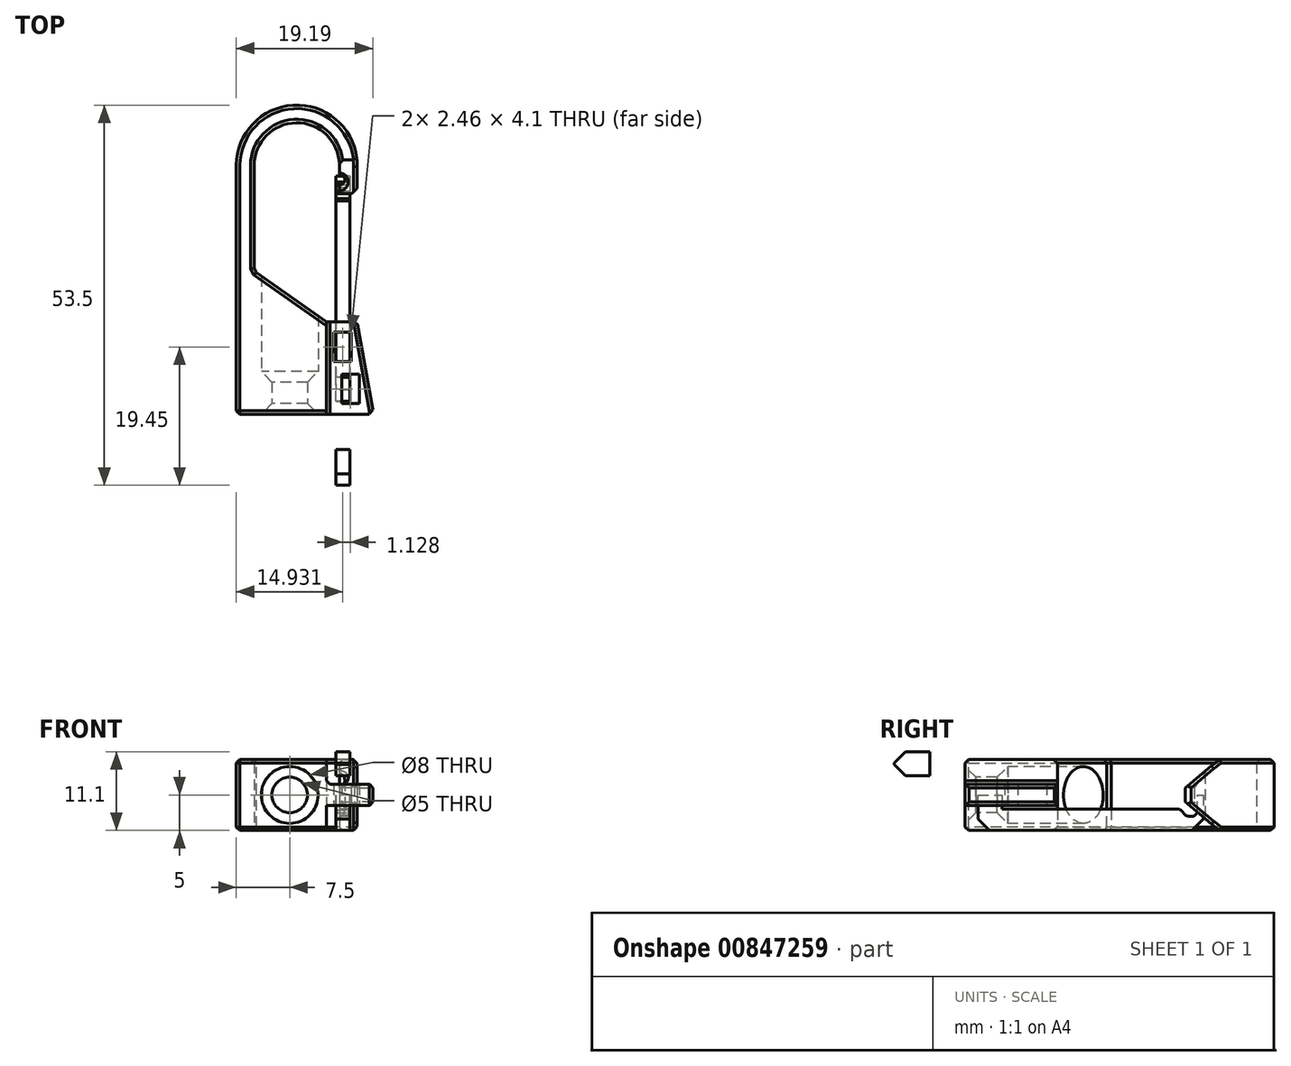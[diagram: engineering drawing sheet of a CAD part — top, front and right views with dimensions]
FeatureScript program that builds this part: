
annotation { "Feature Type Name" : "Feature", "Feature Type Description" : "" }
export const myFeature = defineFeature(function(context is Context, id is Id, definition is map)
    precondition{}
    {
        {
            var Q0;
            Q0=qCreatedBy(makeId("Top.planeOp"),FACE);
            var sketch = newSketch(context, id + "F0", { "sketchPlane" : qUnion([Q0])});
            skCircle(sketch, "E0", {"center": v(-1, -1.5) * mm, "radius": 4 * mm});
            skLineSegment(sketch, "E1.bottom", {"start": v(-8.5, 3.5) * mm, "end": v(8.5, 3.5) * mm});
            skLineSegment(sketch, "E1.top", {"start": v(-8.5, -6.5) * mm, "end": v(8.5, -6.5) * mm});
            skLineSegment(sketch, "E1.left", {"start": v(-8.5, 3.5) * mm, "end": v(-8.5, -6.5) * mm});
            skLineSegment(sketch, "E1.right", {"start": v(8.5, 3.5) * mm, "end": v(8.5, -6.5) * mm});
            skPoint(sketch, "E1.middle", {"position": v(0, -1.5) * mm});
            skCircle(sketch, "E2", {"center": v(-1, -1.5) * mm, "radius": 2.5 * mm});
            skSolve(sketch);
        }
        {
            var Q0;
            Q0=qCreatedBy(makeId("Front.planeOp"),FACE);
            cPlane(context, id + "F1", {"entities" : qUnion([Q0]), "cplaneType" : CPlaneType.OFFSET, "offset" : 3.5 * mm, "oppositeDirection" : true, "width" : 150 * mm, "height" : 150 * mm});
        }
        {
            var Q0;
            Q0=qCreatedBy(id+"F1.planeOp",FACE);
            var sketch = newSketch(context, id + "F2", { "sketchPlane" : qUnion([Q0])});
            skLineSegment(sketch, "E3", {"start": v(0, 0) * mm, "end": v(8.5, 0) * mm});
            skLineSegment(sketch, "E4.MirrorCS", {"start": v(0, 0) * mm, "end": v(-8.5, 0) * mm});
            skLineSegment(sketch, "E5", {"start": v(8.5, 0) * mm, "end": v(8.5, 13) * mm});
            skLineSegment(sketch, "E6", {"start": v(8.5, 13) * mm, "end": v(4.2, 13) * mm});
            skLineSegment(sketch, "E7", {"start": v(4.2, 13) * mm, "end": v(-6, 20.14) * mm});
            skLineSegment(sketch, "E8", {"start": v(-8.5, 0) * mm, "end": v(-8.5, 35) * mm});
            skLineSegment(sketch, "E9", {"start": v(-6, 20.14) * mm, "end": v(-6, 35) * mm});
            skLineSegment(sketch, "E10", {"start": v(-6, 35) * mm, "end": v(0, 35) * mm});
            skArc(sketch, "E11", {"start": v(8.5, 35) * mm, "mid": v(0, 43.5) * mm, "end": v(-8.5, 35) * mm});
            skArc(sketch, "E12", {"start": v(6, 35) * mm, "mid": v(0, 41) * mm, "end": v(-6, 35) * mm});
            skLineSegment(sketch, "E13", {"start": v(0, 35) * mm, "end": v(8.5, 35) * mm});
            skLineSegment(sketch, "E14", {"start": v(6, 35) * mm, "end": v(6, 31) * mm});
            skLineSegment(sketch, "E15.bottom", {"start": v(6, 31) * mm, "end": v(8.5, 31) * mm});
            skLineSegment(sketch, "E15.top", {"start": v(6, 35) * mm, "end": v(8.5, 35) * mm});
            skLineSegment(sketch, "E15.left", {"start": v(6, 31) * mm, "end": v(6, 35) * mm});
            skLineSegment(sketch, "E15.right", {"start": v(8.5, 31) * mm, "end": v(8.5, 35) * mm});
            skCircle(sketch, "E16", {"center": v(8.5, 33) * mm, "radius": 0.75 * mm});
            skLineSegment(sketch, "E17", {"start": v(8.5, 13) * mm, "end": v(10.8, 0) * mm});
            skLineSegment(sketch, "E18", {"start": v(10.8, 0) * mm, "end": v(8.5, 0) * mm});
            skLineSegment(sketch, "E19", {"start": v(4.2, 13) * mm, "end": v(4.2, 0) * mm});
            skLineSegment(sketch, "E20.0", {"start": v(5.2, 12) * mm, "end": v(5.2, 0) * mm});
            skLineSegment(sketch, "E20.1", {"start": v(7.66, 12) * mm, "end": v(5.2, 12) * mm});
            skLineSegment(sketch, "E20.2", {"start": v(7.66, 12) * mm, "end": v(9.6, 1) * mm});
            skLineSegment(sketch, "E20.3", {"start": v(9.6, 1) * mm, "end": v(8.5, 1) * mm});
            skLineSegment(sketch, "E21", {"start": v(8.5, 1) * mm, "end": v(5.2, 1) * mm});
            skLineSegment(sketch, "E22", {"start": v(5.2, 12) * mm, "end": v(7.14, 1) * mm});
            skCircle(sketch, "E23", {"center": v(6, 33) * mm, "radius": 0.75 * mm});
            skLineSegment(sketch, "E24.0", {"start": v(8.5, 11.5) * mm, "end": v(4.2, 11.5) * mm});
            skLineSegment(sketch, "E25.0", {"start": v(0, 1.5) * mm, "end": v(8.5, 1.5) * mm});
            skLineSegment(sketch, "E25.1", {"start": v(10.8, 1.5) * mm, "end": v(8.5, 1.5) * mm});
            skLineSegment(sketch, "E26", {"start": v(8.79, 5.6) * mm, "end": v(8.79, 1) * mm});
            skLineSegment(sketch, "E27", {"start": v(8.79, 5.6) * mm, "end": v(6.33, 5.6) * mm});
            skLineSegment(sketch, "E28", {"start": v(7.66, 12) * mm, "end": v(7.66, 7.4) * mm});
            skLineSegment(sketch, "E29", {"start": v(7.66, 7.4) * mm, "end": v(5.2, 7.4) * mm});
            skLineSegment(sketch, "E30", {"start": v(6.33, 5.6) * mm, "end": v(6.33, 1) * mm});
            skSolve(sketch);
        }
        {
            var Q0;
            {var subQ1=sQuery(id+"F2.wireOp",EDGE,"E6");Q0=makeQuery(id+"F2.imprint","IMPRINT",FACE,{"disambiguationData":[TD([[makeQuery(id+"F2.imprint","IMPRINT",EDGE,{"derivedFrom":subQ1}),1.0]])]});}
            var Q1;
            {var subQ0=sQuery(id+"F2.wireOp",EDGE,"E24.0");var subQ1=sQuery(id+"F2.wireOp",EDGE,"E19");var subQ2=makeQuery(id+"F2.imprint","INTERSECT",VERTEX,{"derivedFrom":[subQ1,subQ0]});Q1=makeQuery(id+"F2.imprint","IMPRINT",FACE,{"disambiguationData":[TD([[makeQuery(id+"F2.imprint","IMPRINT",EDGE,{"disambiguationData":[TD([[subQ2,-1.0]])],"derivedFrom":subQ1}),1.0]])]});}
            var Q2;
            {var subQ4=sQuery(id+"F2.wireOp",EDGE,"E3");var subQ6=sQuery(id+"F2.wireOp",EDGE,"E19");var subQ7=makeQuery(id+"F2.imprint","INTERSECT",VERTEX,{"derivedFrom":[subQ4,subQ6]});Q2=makeQuery(id+"F2.imprint","IMPRINT",FACE,{"disambiguationData":[TD([[makeQuery(id+"F2.imprint","IMPRINT",EDGE,{"disambiguationData":[TD([[subQ7,-1.0]])],"derivedFrom":subQ4}),1.0]])]});}
            var Q3;
            {var subQ0=sQuery(id+"F2.wireOp",EDGE,"E20.0");var subQ1=sQuery(id+"F2.wireOp",EDGE,"E3");var subQ2=makeQuery(id+"F2.imprint","INTERSECT",VERTEX,{"derivedFrom":[subQ1,subQ0]});Q3=makeQuery(id+"F2.imprint","IMPRINT",FACE,{"disambiguationData":[TD([[makeQuery(id+"F2.imprint","IMPRINT",EDGE,{"disambiguationData":[TD([[subQ2,1.0]])],"derivedFrom":subQ0}),1.0]])]});}
            var Q4;
            {var subQ0=sQuery(id+"F2.wireOp",EDGE,"E18");Q4=makeQuery(id+"F2.imprint","IMPRINT",FACE,{"disambiguationData":[TD([[makeQuery(id+"F2.imprint","IMPRINT",EDGE,{"derivedFrom":subQ0}),-1.0]])]});}
            var Q5;
            {var subQ2=sQuery(id+"F2.wireOp",EDGE,"E5");var subQ6=makeQuery(id+"F2.imprint","INTERSECT",VERTEX,{"derivedFrom":[subQ2,sQuery(id+"F2.wireOp",EDGE,"E24.0")]});Q5=makeQuery(id+"F2.imprint","IMPRINT",FACE,{"disambiguationData":[TD([[makeQuery(id+"F2.imprint","IMPRINT",EDGE,{"disambiguationData":[TD([[subQ6,1.0]])],"derivedFrom":subQ2}),-1.0]])]});}
            var Q6;
            {var subQ4=sQuery(id+"F2.wireOp",EDGE,"E4.MirrorCS");Q6=makeQuery(id+"F2.imprint","IMPRINT",FACE,{"disambiguationData":[TD([[makeQuery(id+"F2.imprint","IMPRINT",EDGE,{"derivedFrom":subQ4}),-1.0]])]});}
            var Q7;
            {var subQ5=sQuery(id+"F2.wireOp",EDGE,"E5");var subQ7=sQuery(id+"F2.wireOp",EDGE,"E27");var subQ13=makeQuery(id+"F2.imprint","INTERSECT",VERTEX,{"derivedFrom":[subQ5,subQ7]});Q7=makeQuery(id+"F2.imprint","IMPRINT",FACE,{"disambiguationData":[TD([[makeQuery(id+"F2.imprint","IMPRINT",EDGE,{"disambiguationData":[TD([[subQ13,-1.0]])],"derivedFrom":subQ5}),1.0]])]});}
            var Q8;
            {var subQ1=sQuery(id+"F2.wireOp",EDGE,"E20.0");var subQ7=sQuery(id+"F2.wireOp",EDGE,"E29");var subQ9=makeQuery(id+"F2.imprint","INTERSECT",VERTEX,{"derivedFrom":[subQ1,subQ7]});Q8=makeQuery(id+"F2.imprint","IMPRINT",FACE,{"disambiguationData":[TD([[makeQuery(id+"F2.imprint","IMPRINT",EDGE,{"disambiguationData":[TD([[subQ9,-1.0]])],"derivedFrom":subQ1}),1.0]])]});}
            var Q9;
            {var subQ1=sQuery(id+"F2.wireOp",EDGE,"E20.2");var subQ3=sQuery(id+"F2.wireOp",EDGE,"E24.0");var subQ4=makeQuery(id+"F2.imprint","INTERSECT",VERTEX,{"derivedFrom":[subQ1,subQ3]});Q9=makeQuery(id+"F2.imprint","IMPRINT",FACE,{"disambiguationData":[TD([[makeQuery(id+"F2.imprint","IMPRINT",EDGE,{"disambiguationData":[TD([[subQ4,-1.0]])],"derivedFrom":subQ3}),-1.0]])]});}
            var Q10;
            {var subQ0=sQuery(id+"F2.wireOp",EDGE,"E24.0");var subQ1=sQuery(id+"F2.wireOp",EDGE,"E5");var subQ2=makeQuery(id+"F2.imprint","INTERSECT",VERTEX,{"derivedFrom":[subQ1,subQ0]});Q10=makeQuery(id+"F2.imprint","IMPRINT",FACE,{"disambiguationData":[TD([[makeQuery(id+"F2.imprint","IMPRINT",EDGE,{"disambiguationData":[TD([[subQ2,1.0]])],"derivedFrom":subQ1}),1.0]])]});}
            var Q11;
            {var subQ0=sQuery(id+"F2.wireOp",EDGE,"E21");var subQ1=sQuery(id+"F2.wireOp",EDGE,"E20.0");var subQ2=makeQuery(id+"F2.imprint","INTERSECT",VERTEX,{"derivedFrom":[subQ1,subQ0]});Q11=makeQuery(id+"F2.imprint","IMPRINT",FACE,{"disambiguationData":[TD([[makeQuery(id+"F2.imprint","IMPRINT",EDGE,{"disambiguationData":[TD([[subQ2,1.0]])],"derivedFrom":subQ1}),1.0]])]});}
            var Q12;
            {var subQ4=sQuery(id+"F2.wireOp",EDGE,"E15.bottom");Q12=makeQuery(id+"F2.imprint","IMPRINT",FACE,{"disambiguationData":[TD([[makeQuery(id+"F2.imprint","IMPRINT",EDGE,{"derivedFrom":subQ4}),1.0]])]});}
            var Q13;
            {var subQ0=sQuery(id+"F2.wireOp",EDGE,"E16");var subQ1=sQuery(id+"F2.wireOp",EDGE,"E15.right");var subQ2=makeQuery(id+"F2.imprint","INTERSECT",VERTEX,{"disambiguationData":[OD(0.0)],"derivedFrom":[subQ1,subQ0]});Q13=makeQuery(id+"F2.imprint","IMPRINT",FACE,{"disambiguationData":[TD([[makeQuery(id+"F2.imprint","IMPRINT",EDGE,{"disambiguationData":[TD([[subQ2,-1.0]])],"derivedFrom":subQ1}),1.0]])]});}
            var Q14;
            {var subQ1=sQuery(id+"F2.wireOp",EDGE,"E20.2");var subQ3=sQuery(id+"F2.wireOp",EDGE,"E25.1");var subQ4=makeQuery(id+"F2.imprint","INTERSECT",VERTEX,{"derivedFrom":[subQ1,subQ3]});Q14=makeQuery(id+"F2.imprint","IMPRINT",FACE,{"disambiguationData":[TD([[makeQuery(id+"F2.imprint","IMPRINT",EDGE,{"disambiguationData":[TD([[subQ4,-1.0]])],"derivedFrom":subQ3}),-1.0]])]});}
            var Q15;
            {var subQ0=sQuery(id+"F2.wireOp",EDGE,"E20.3");var subQ1=sQuery(id+"F2.wireOp",EDGE,"E20.2");var subQ2=makeQuery(id+"F2.imprint","INTERSECT",VERTEX,{"derivedFrom":[subQ1,subQ0]});Q15=makeQuery(id+"F2.imprint","IMPRINT",FACE,{"disambiguationData":[TD([[makeQuery(id+"F2.imprint","IMPRINT",EDGE,{"disambiguationData":[TD([[subQ2,1.0]])],"derivedFrom":subQ1}),-1.0]])]});}
            var Q16;
            {var subQ0=sQuery(id+"F2.wireOp",EDGE,"E27");var subQ1=sQuery(id+"F2.wireOp",EDGE,"E5");var subQ2=makeQuery(id+"F2.imprint","INTERSECT",VERTEX,{"derivedFrom":[subQ1,subQ0]});Q16=makeQuery(id+"F2.imprint","IMPRINT",FACE,{"disambiguationData":[TD([[makeQuery(id+"F2.imprint","IMPRINT",EDGE,{"disambiguationData":[TD([[subQ2,-1.0]])],"derivedFrom":subQ1}),-1.0]])]});}
            var Q17;
            {var subQ0=sQuery(id+"F2.wireOp",EDGE,"E22");var subQ1=sQuery(id+"F2.wireOp",EDGE,"E21");var subQ2=makeQuery(id+"F2.imprint","INTERSECT",VERTEX,{"derivedFrom":[subQ1,subQ0]});Q17=makeQuery(id+"F2.imprint","IMPRINT",FACE,{"disambiguationData":[TD([[makeQuery(id+"F2.imprint","IMPRINT",EDGE,{"disambiguationData":[TD([[subQ2,-1.0]])],"derivedFrom":subQ1}),-1.0]])]});}
            var Q18;
            {var subQ0=sQuery(id+"F2.wireOp",EDGE,"E21");var subQ5=sQuery(id+"F2.wireOp",EDGE,"E22");var subQ7=makeQuery(id+"F2.imprint","INTERSECT",VERTEX,{"derivedFrom":[subQ0,subQ5]});Q18=makeQuery(id+"F2.imprint","IMPRINT",FACE,{"disambiguationData":[TD([[makeQuery(id+"F2.imprint","IMPRINT",EDGE,{"disambiguationData":[TD([[subQ7,1.0]])],"derivedFrom":subQ5}),1.0]])]});}
            var Q19;
            {var subQ0=sQuery(id+"F2.wireOp",EDGE,"E20.3");var subQ5=sQuery(id+"F2.wireOp",EDGE,"E26");var subQ6=makeQuery(id+"F2.imprint","INTERSECT",VERTEX,{"derivedFrom":[subQ0,subQ5]});Q19=makeQuery(id+"F2.imprint","IMPRINT",FACE,{"disambiguationData":[TD([[makeQuery(id+"F2.imprint","IMPRINT",EDGE,{"disambiguationData":[TD([[subQ6,1.0]])],"derivedFrom":subQ5}),-1.0]])]});}
            var Q20;
            {var subQ0=sQuery(id+"F2.wireOp",EDGE,"E20.1");Q20=makeQuery(id+"F2.imprint","IMPRINT",FACE,{"disambiguationData":[TD([[makeQuery(id+"F2.imprint","IMPRINT",EDGE,{"derivedFrom":subQ0}),1.0]])]});}
            var Q21;
            {var subQ1=sQuery(id+"F2.wireOp",EDGE,"E20.0");var subQ3=sQuery(id+"F2.wireOp",EDGE,"E24.0");var subQ4=makeQuery(id+"F2.imprint","INTERSECT",VERTEX,{"derivedFrom":[subQ1,subQ3]});Q21=makeQuery(id+"F2.imprint","IMPRINT",FACE,{"disambiguationData":[TD([[makeQuery(id+"F2.imprint","IMPRINT",EDGE,{"disambiguationData":[TD([[subQ4,1.0]])],"derivedFrom":subQ3}),-1.0]])]});}
            var Q22;
            {var subQ1=sQuery(id+"F2.wireOp",EDGE,"E20.2");var subQ3=sQuery(id+"F2.wireOp",EDGE,"E24.0");var subQ4=makeQuery(id+"F2.imprint","INTERSECT",VERTEX,{"derivedFrom":[subQ1,subQ3]});Q22=makeQuery(id+"F2.imprint","IMPRINT",FACE,{"disambiguationData":[TD([[makeQuery(id+"F2.imprint","IMPRINT",EDGE,{"disambiguationData":[TD([[subQ4,-1.0]])],"derivedFrom":subQ3}),-1.0]])]});}
            extrude(context, id + "F3", {"entities" : qUnion([Q0, Q1, Q2, Q3, Q4, Q5, Q6, Q7, Q8, Q9, Q10, Q11, Q12, Q13, Q14, Q15, Q16, Q17, Q18, Q19, Q20, Q21, Q22]), "depth" : 10 * mm, "offsetDistance" : 25 * mm});
        }
        {
            var Q0;
            Q0=makeQuery(id+"F0.imprint","IMPRINT",FACE,{"disambiguationData":[TD([[makeQuery(id+"F0.imprint","IMPRINT",EDGE,{"derivedFrom":sQuery(id+"F0.wireOp",EDGE,"E0")}),1.0]])]});
            var Q1;
            Q1=makeQuery(id+"F0.imprint","IMPRINT",FACE,{"disambiguationData":[TD([[makeQuery(id+"F0.imprint","IMPRINT",EDGE,{"derivedFrom":sQuery(id+"F0.wireOp",EDGE,"E2")}),1.0]])]});
            extrude(context, id + "F4", {"entities" : qUnion([Q0, Q1]), "operationType" : NewBodyOperationType.REMOVE, "depth" : 25 * mm, "offsetDistance" : 25 * mm});
        }
        {
            var Q0;
            Q0=makeQuery(id+"F0.imprint","IMPRINT",FACE,{"disambiguationData":[TD([[makeQuery(id+"F0.imprint","IMPRINT",EDGE,{"derivedFrom":sQuery(id+"F0.wireOp",EDGE,"E0")}),1.0]])]});
            extrude(context, id + "F5", {"entities" : qUnion([Q0]), "operationType" : NewBodyOperationType.ADD, "depth" : 6 * mm, "offsetDistance" : 25 * mm});
        }
        {
            var Q0;
            Q0=makeQuery(id+"F3.opExtrude","CAP_EDGE",EDGE,{"disambiguationData":[OSD([sQuery(id+"F2.wireOp",EDGE,"E15.bottom")])],"isStart":false});
            var Q1;
            Q1=makeQuery(id+"F3.opExtrude","CAP_EDGE",EDGE,{"disambiguationData":[OSD([sQuery(id+"F2.wireOp",EDGE,"E15.bottom")])],"isStart":true});
            chamfer(context, id + "F6", {"entities" : qUnion([Q0, Q1]), "chamferType" : ChamferType.OFFSET_ANGLE, "width" : 4 * mm, "oppositeDirection" : true, "angle" : 50 * degree, "tangentPropagation" : true});
        }
        {
            var Q0;
            Q0=makeQuery(id+"F5.opExtrude","CAP_EDGE",EDGE,{"disambiguationData":[OSD([sQuery(id+"F0.wireOp",EDGE,"E2")])],"isStart":true});
            var Q1;
            Q1=makeQuery(id+"F5.opExtrude","CAP_EDGE",EDGE,{"disambiguationData":[OSD([sQuery(id+"F0.wireOp",EDGE,"E2")])],"isStart":false});
            chamfer(context, id + "F7", {"entities" : qUnion([Q0, Q1]), "width" : 1.5 * mm, "tangentPropagation" : true});
        }
        {
            var Q0;
            Q0=makeQuery(id+"F3.opExtrude","SWEPT_EDGE",EDGE,{"disambiguationData":[OSD([sQuery(id+"F2.wireOp",EDGE,"E7"),sQuery(id+"F2.wireOp",EDGE,"E9")])]});
            var Q1;
            Q1=makeQuery(id+"F3.opExtrude","SWEPT_EDGE",EDGE,{"disambiguationData":[OSD([sQuery(id+"F2.wireOp",EDGE,"E15.bottom"),sQuery(id+"F2.wireOp",EDGE,"E15.right")])]});
            chamfer(context, id + "F8", {"entities" : qUnion([Q0, Q1]), "width" : .8 * mm, "tangentPropagation" : true});
        }
        {
            var Q0;
            Q0=qCreatedBy(id+"F1.planeOp",FACE);
            var sketch = newSketch(context, id + "F9", { "sketchPlane" : qUnion([Q0])});
            skLineSegment(sketch, "E31", {"start": v(0, 0) * mm, "end": v(4.2, 0) * mm});
            skLineSegment(sketch, "E32", {"start": v(4.2, 0) * mm, "end": v(11.2, 0) * mm});
            skLineSegment(sketch, "E33", {"start": v(4.2, 0) * mm, "end": v(4.2, 15.17) * mm});
            skLineSegment(sketch, "E34.bottom", {"start": v(4.2, 15.17) * mm, "end": v(11.2, 15.17) * mm});
            skLineSegment(sketch, "E34.left", {"start": v(4.2, 15.17) * mm, "end": v(4.2, 0) * mm});
            skLineSegment(sketch, "E34.right", {"start": v(11.2, 15.17) * mm, "end": v(11.2, 0) * mm});
            skSolve(sketch);
        }
        {
            var Q0;
            Q0=qSketchRegion(id+"F9",true);
            extrude(context, id + "F10", {"entities" : qUnion([Q0]), "operationType" : NewBodyOperationType.REMOVE, "depth" : 3.5 * mm, "offsetDistance" : 25 * mm});
        }
        {
            var Q0;
            Q0=qCreatedBy(id+"F1.planeOp",FACE);
            cPlane(context, id + "F11", {"entities" : qUnion([Q0]), "cplaneType" : CPlaneType.OFFSET, "offset" : 10 * mm, "width" : 150 * mm, "height" : 150 * mm});
        }
        {
            var Q0;
            Q0=qCreatedBy(id+"F11.planeOp",FACE);
            var sketch = newSketch(context, id + "F12", { "sketchPlane" : qUnion([Q0])});
            skLineSegment(sketch, "E35", {"start": v(0, 0) * mm, "end": v(4.2, 0) * mm});
            skLineSegment(sketch, "E36", {"start": v(4.2, 0) * mm, "end": v(11.2, 0) * mm});
            skLineSegment(sketch, "E37", {"start": v(11.2, 0) * mm, "end": v(11.2, 14.54) * mm});
            skLineSegment(sketch, "E38.bottom", {"start": v(11.2, 14.54) * mm, "end": v(4.2, 14.54) * mm});
            skLineSegment(sketch, "E38.top", {"start": v(11.2, 0) * mm, "end": v(4.2, 0) * mm});
            skLineSegment(sketch, "E38.left", {"start": v(11.2, 14.54) * mm, "end": v(11.2, 0) * mm});
            skLineSegment(sketch, "E38.right", {"start": v(4.2, 14.54) * mm, "end": v(4.2, 0) * mm});
            skSolve(sketch);
        }
        {
            var Q0;
            Q0=qSketchRegion(id+"F12",true);
            extrude(context, id + "F13", {"entities" : qUnion([Q0]), "operationType" : NewBodyOperationType.REMOVE, "oppositeDirection" : true, "depth" : 3.5 * mm, "offsetDistance" : 25 * mm});
        }
        {
            var Q0;
            Q0=makeQuery(id+"F13.boolean.opBoolean","INTERSECT",EDGE,{"derivedFrom":[makeQuery(id+"F3.opExtrude","SWEPT_FACE",FACE,{"disambiguationData":[OSD([sQuery(id+"F2.wireOp",EDGE,"E17")])]}),makeQuery(id+"F13.opExtrude","CAP_FACE",FACE,{"disambiguationData":[OSD([sQuery(id+"F12.wireOp",EDGE,"E38.bottom"),sQuery(id+"F12.wireOp",EDGE,"E38.top"),sQuery(id+"F12.wireOp",EDGE,"E38.left"),sQuery(id+"F12.wireOp",EDGE,"E38.right")])],"isStart":false})]});
            var Q1;
            Q1=makeQuery(id+"F10.boolean.opBoolean","INTERSECT",EDGE,{"derivedFrom":[makeQuery(id+"F3.opExtrude","SWEPT_FACE",FACE,{"disambiguationData":[OSD([sQuery(id+"F2.wireOp",EDGE,"E17")])]}),makeQuery(id+"F10.opExtrude","CAP_FACE",FACE,{"disambiguationData":[OSD([sQuery(id+"F9.wireOp",EDGE,"E34.bottom"),sQuery(id+"F9.wireOp",EDGE,"E32"),sQuery(id+"F9.wireOp",EDGE,"E34.left"),sQuery(id+"F9.wireOp",EDGE,"E34.right")])],"isStart":false})]});
            var Q2;
            Q2=makeQuery(id+"F3.opExtrude","CAP_EDGE",EDGE,{"disambiguationData":[OSD([sQuery(id+"F2.wireOp",EDGE,"E8")])],"isStart":false});
            var Q3;
            Q3=makeQuery(id+"F3.opExtrude","CAP_EDGE",EDGE,{"disambiguationData":[OSD([sQuery(id+"F2.wireOp",EDGE,"E8")])],"isStart":true});
            var Q4;
            Q4=makeQuery(id+"F3.opExtrude","CAP_EDGE",EDGE,{"disambiguationData":[OSD([sQuery(id+"F2.wireOp",EDGE,"E9")])],"isStart":true});
            var Q5;
            Q5=makeQuery(id+"F3.opExtrude","CAP_EDGE",EDGE,{"disambiguationData":[OSD([sQuery(id+"F2.wireOp",EDGE,"E9")])],"isStart":false});
            var Q6;
            Q6=makeQuery(id+"F3.opExtrude","CAP_EDGE",EDGE,{"disambiguationData":[OSD([sQuery(id+"F2.wireOp",EDGE,"E7")])],"isStart":false});
            var Q7;
            Q7=makeQuery(id+"F3.opExtrude","CAP_EDGE",EDGE,{"disambiguationData":[OSD([sQuery(id+"F2.wireOp",EDGE,"E7")])],"isStart":true});
            var Q8;
            {var subQ0=sQuery(id+"F2.wireOp",EDGE,"E9");var subQ1=sQuery(id+"F2.wireOp",EDGE,"E7");Q8=makeQuery(id+"F8.opChamfer","BLEND_EDGE",EDGE,{"blendedFrom":[makeQuery(id+"F3.opExtrude","SWEPT_EDGE",EDGE,{"disambiguationData":[OSD([subQ1,subQ0])]}),makeQuery(id+"F3.opExtrude","CAP_FACE",FACE,{"disambiguationData":[OSD([sQuery(id+"F2.wireOp",EDGE,"E3"),sQuery(id+"F2.wireOp",EDGE,"E4.MirrorCS"),sQuery(id+"F2.wireOp",EDGE,"E6"),subQ1,sQuery(id+"F2.wireOp",EDGE,"E8"),subQ0,sQuery(id+"F2.wireOp",EDGE,"E11"),sQuery(id+"F2.wireOp",EDGE,"E12"),sQuery(id+"F2.wireOp",EDGE,"E15.bottom"),sQuery(id+"F2.wireOp",EDGE,"E15.left"),sQuery(id+"F2.wireOp",EDGE,"E15.right"),sQuery(id+"F2.wireOp",EDGE,"E16"),sQuery(id+"F2.wireOp",EDGE,"E17"),sQuery(id+"F2.wireOp",EDGE,"E18")])],"isStart":true})],"blendedInto":[makeQuery(id+"F3.opExtrude","CAP_FACE",FACE,{"disambiguationData":[OSD([sQuery(id+"F2.wireOp",EDGE,"E3"),sQuery(id+"F2.wireOp",EDGE,"E4.MirrorCS"),sQuery(id+"F2.wireOp",EDGE,"E6"),subQ1,sQuery(id+"F2.wireOp",EDGE,"E8"),subQ0,sQuery(id+"F2.wireOp",EDGE,"E11"),sQuery(id+"F2.wireOp",EDGE,"E12"),sQuery(id+"F2.wireOp",EDGE,"E15.bottom"),sQuery(id+"F2.wireOp",EDGE,"E15.left"),sQuery(id+"F2.wireOp",EDGE,"E15.right"),sQuery(id+"F2.wireOp",EDGE,"E16"),sQuery(id+"F2.wireOp",EDGE,"E17"),sQuery(id+"F2.wireOp",EDGE,"E18")])],"isStart":true})]});}
            var Q9;
            {var subQ0=sQuery(id+"F2.wireOp",EDGE,"E9");var subQ1=sQuery(id+"F2.wireOp",EDGE,"E7");Q9=makeQuery(id+"F8.opChamfer","BLEND_EDGE",EDGE,{"blendedFrom":[makeQuery(id+"F3.opExtrude","SWEPT_EDGE",EDGE,{"disambiguationData":[OSD([subQ1,subQ0])]}),makeQuery(id+"F3.opExtrude","CAP_FACE",FACE,{"disambiguationData":[OSD([sQuery(id+"F2.wireOp",EDGE,"E3"),sQuery(id+"F2.wireOp",EDGE,"E4.MirrorCS"),sQuery(id+"F2.wireOp",EDGE,"E6"),subQ1,sQuery(id+"F2.wireOp",EDGE,"E8"),subQ0,sQuery(id+"F2.wireOp",EDGE,"E11"),sQuery(id+"F2.wireOp",EDGE,"E12"),sQuery(id+"F2.wireOp",EDGE,"E15.bottom"),sQuery(id+"F2.wireOp",EDGE,"E15.left"),sQuery(id+"F2.wireOp",EDGE,"E15.right"),sQuery(id+"F2.wireOp",EDGE,"E16"),sQuery(id+"F2.wireOp",EDGE,"E17"),sQuery(id+"F2.wireOp",EDGE,"E18")])],"isStart":false})],"blendedInto":[makeQuery(id+"F3.opExtrude","CAP_FACE",FACE,{"disambiguationData":[OSD([sQuery(id+"F2.wireOp",EDGE,"E3"),sQuery(id+"F2.wireOp",EDGE,"E4.MirrorCS"),sQuery(id+"F2.wireOp",EDGE,"E6"),subQ1,sQuery(id+"F2.wireOp",EDGE,"E8"),subQ0,sQuery(id+"F2.wireOp",EDGE,"E11"),sQuery(id+"F2.wireOp",EDGE,"E12"),sQuery(id+"F2.wireOp",EDGE,"E15.bottom"),sQuery(id+"F2.wireOp",EDGE,"E15.left"),sQuery(id+"F2.wireOp",EDGE,"E15.right"),sQuery(id+"F2.wireOp",EDGE,"E16"),sQuery(id+"F2.wireOp",EDGE,"E17"),sQuery(id+"F2.wireOp",EDGE,"E18")])],"isStart":false})]});}
            var Q10;
            Q10=makeQuery(id+"F6.opChamfer","BLEND_EDGE",EDGE,{"blendedFrom":[makeQuery(id+"F3.opExtrude","CAP_EDGE",EDGE,{"disambiguationData":[OSD([sQuery(id+"F2.wireOp",EDGE,"E15.bottom")])],"isStart":false}),makeQuery(id+"F3.opExtrude","SWEPT_FACE",FACE,{"disambiguationData":[OSD([sQuery(id+"F2.wireOp",EDGE,"E15.left")])]})],"blendedInto":[makeQuery(id+"F3.opExtrude","SWEPT_FACE",FACE,{"disambiguationData":[OSD([sQuery(id+"F2.wireOp",EDGE,"E15.left")])]})]});
            var Q11;
            Q11=makeQuery(id+"F6.opChamfer","BLEND_EDGE",EDGE,{"blendedFrom":[makeQuery(id+"F3.opExtrude","CAP_EDGE",EDGE,{"disambiguationData":[OSD([sQuery(id+"F2.wireOp",EDGE,"E15.bottom")])],"isStart":true}),makeQuery(id+"F3.opExtrude","SWEPT_FACE",FACE,{"disambiguationData":[OSD([sQuery(id+"F2.wireOp",EDGE,"E15.left")])]})],"blendedInto":[makeQuery(id+"F3.opExtrude","SWEPT_FACE",FACE,{"disambiguationData":[OSD([sQuery(id+"F2.wireOp",EDGE,"E15.left")])]})]});
            var Q12;
            {var subQ0=sQuery(id+"F2.wireOp",EDGE,"E15.right");Q12=makeQuery(id+"F6.opChamfer","BLEND_EDGE",EDGE,{"blendedFrom":[makeQuery(id+"F3.opExtrude","CAP_EDGE",EDGE,{"disambiguationData":[OSD([sQuery(id+"F2.wireOp",EDGE,"E15.bottom")])],"isStart":false}),makeQuery(id+"F3.opExtrude","SWEPT_FACE",FACE,{"disambiguationData":[OSD([subQ0]),TDD([makeQuery(id+"F2.imprint","IMPRINT",EDGE,{"disambiguationData":[TD([[makeQuery(id+"F2.imprint","INTERSECT",VERTEX,{"disambiguationData":[OD(1.0)],"derivedFrom":[subQ0,sQuery(id+"F2.wireOp",EDGE,"E16")]}),-1.0]])],"derivedFrom":subQ0})])]})],"blendedInto":[makeQuery(id+"F3.opExtrude","SWEPT_FACE",FACE,{"disambiguationData":[OSD([subQ0]),TDD([makeQuery(id+"F2.imprint","IMPRINT",EDGE,{"disambiguationData":[TD([[makeQuery(id+"F2.imprint","INTERSECT",VERTEX,{"disambiguationData":[OD(1.0)],"derivedFrom":[subQ0,sQuery(id+"F2.wireOp",EDGE,"E16")]}),-1.0]])],"derivedFrom":subQ0})])]})]});}
            var Q13;
            Q13=makeQuery(id+"F6.opChamfer","BLEND_EDGE",EDGE,{"blendedFrom":[makeQuery(id+"F3.opExtrude","CAP_EDGE",EDGE,{"disambiguationData":[OSD([sQuery(id+"F2.wireOp",EDGE,"E15.bottom")])],"isStart":false}),makeQuery(id+"F3.opExtrude","SWEPT_FACE",FACE,{"disambiguationData":[OSD([sQuery(id+"F2.wireOp",EDGE,"E16")])]})],"blendedInto":[makeQuery(id+"F3.opExtrude","SWEPT_FACE",FACE,{"disambiguationData":[OSD([sQuery(id+"F2.wireOp",EDGE,"E16")])]})]});
            var Q14;
            {var subQ0=sQuery(id+"F2.wireOp",EDGE,"E15.right");var subQ1=sQuery(id+"F2.wireOp",EDGE,"E15.bottom");Q14=makeQuery(id+"F6.opChamfer","BLEND_EDGE",EDGE,{"blendedFrom":[makeQuery(id+"F3.opExtrude","CAP_EDGE",EDGE,{"disambiguationData":[OSD([subQ1])],"isStart":false}),makeQuery(id+"F3.opExtrude","SWEPT_FACE",FACE,{"disambiguationData":[OSD([subQ0]),TDD([makeQuery(id+"F2.imprint","IMPRINT",EDGE,{"disambiguationData":[TD([[makeQuery(id+"F2.imprint","INTERSECT",VERTEX,{"derivedFrom":[subQ1,subQ0]}),-1.0]])],"derivedFrom":subQ0})])]})],"blendedInto":[makeQuery(id+"F3.opExtrude","SWEPT_FACE",FACE,{"disambiguationData":[OSD([subQ0]),TDD([makeQuery(id+"F2.imprint","IMPRINT",EDGE,{"disambiguationData":[TD([[makeQuery(id+"F2.imprint","INTERSECT",VERTEX,{"derivedFrom":[subQ1,subQ0]}),-1.0]])],"derivedFrom":subQ0})])]})]});}
            var Q15;
            {var subQ0=sQuery(id+"F2.wireOp",EDGE,"E15.right");Q15=makeQuery(id+"F6.opChamfer","BLEND_EDGE",EDGE,{"blendedFrom":[makeQuery(id+"F3.opExtrude","CAP_EDGE",EDGE,{"disambiguationData":[OSD([sQuery(id+"F2.wireOp",EDGE,"E15.bottom")])],"isStart":true}),makeQuery(id+"F3.opExtrude","SWEPT_FACE",FACE,{"disambiguationData":[OSD([subQ0]),TDD([makeQuery(id+"F2.imprint","IMPRINT",EDGE,{"disambiguationData":[TD([[makeQuery(id+"F2.imprint","INTERSECT",VERTEX,{"disambiguationData":[OD(1.0)],"derivedFrom":[subQ0,sQuery(id+"F2.wireOp",EDGE,"E16")]}),-1.0]])],"derivedFrom":subQ0})])]})],"blendedInto":[makeQuery(id+"F3.opExtrude","SWEPT_FACE",FACE,{"disambiguationData":[OSD([subQ0]),TDD([makeQuery(id+"F2.imprint","IMPRINT",EDGE,{"disambiguationData":[TD([[makeQuery(id+"F2.imprint","INTERSECT",VERTEX,{"disambiguationData":[OD(1.0)],"derivedFrom":[subQ0,sQuery(id+"F2.wireOp",EDGE,"E16")]}),-1.0]])],"derivedFrom":subQ0})])]})]});}
            var Q16;
            Q16=makeQuery(id+"F6.opChamfer","BLEND_EDGE",EDGE,{"blendedFrom":[makeQuery(id+"F3.opExtrude","CAP_EDGE",EDGE,{"disambiguationData":[OSD([sQuery(id+"F2.wireOp",EDGE,"E15.bottom")])],"isStart":true}),makeQuery(id+"F3.opExtrude","SWEPT_FACE",FACE,{"disambiguationData":[OSD([sQuery(id+"F2.wireOp",EDGE,"E16")])]})],"blendedInto":[makeQuery(id+"F3.opExtrude","SWEPT_FACE",FACE,{"disambiguationData":[OSD([sQuery(id+"F2.wireOp",EDGE,"E16")])]})]});
            var Q17;
            {var subQ0=sQuery(id+"F2.wireOp",EDGE,"E15.right");var subQ1=sQuery(id+"F2.wireOp",EDGE,"E15.bottom");Q17=makeQuery(id+"F6.opChamfer","BLEND_EDGE",EDGE,{"blendedFrom":[makeQuery(id+"F3.opExtrude","CAP_EDGE",EDGE,{"disambiguationData":[OSD([subQ1])],"isStart":true}),makeQuery(id+"F3.opExtrude","SWEPT_FACE",FACE,{"disambiguationData":[OSD([subQ0]),TDD([makeQuery(id+"F2.imprint","IMPRINT",EDGE,{"disambiguationData":[TD([[makeQuery(id+"F2.imprint","INTERSECT",VERTEX,{"derivedFrom":[subQ1,subQ0]}),-1.0]])],"derivedFrom":subQ0})])]})],"blendedInto":[makeQuery(id+"F3.opExtrude","SWEPT_FACE",FACE,{"disambiguationData":[OSD([subQ0]),TDD([makeQuery(id+"F2.imprint","IMPRINT",EDGE,{"disambiguationData":[TD([[makeQuery(id+"F2.imprint","INTERSECT",VERTEX,{"derivedFrom":[subQ1,subQ0]}),-1.0]])],"derivedFrom":subQ0})])]})]});}
            var Q18;
            Q18=makeQuery(id+"F10.boolean.opBoolean","COPY",EDGE,{"derivedFrom":makeQuery(id+"F10.opExtrude","CAP_EDGE",EDGE,{"disambiguationData":[OSD([sQuery(id+"F9.wireOp",EDGE,"E34.left")])],"isStart":true})});
            var Q19;
            Q19=makeQuery(id+"F13.boolean.opBoolean","COPY",EDGE,{"derivedFrom":makeQuery(id+"F13.opExtrude","CAP_EDGE",EDGE,{"disambiguationData":[OSD([sQuery(id+"F12.wireOp",EDGE,"E38.right")])],"isStart":true})});
            var Q20;
            Q20=makeQuery(id+"F13.boolean.opBoolean","COPY",EDGE,{"derivedFrom":makeQuery(id+"F13.opExtrude","CAP_EDGE",EDGE,{"disambiguationData":[OSD([sQuery(id+"F12.wireOp",EDGE,"E38.right")])],"isStart":false})});
            var Q21;
            Q21=makeQuery(id+"F10.boolean.opBoolean","COPY",EDGE,{"derivedFrom":makeQuery(id+"F10.opExtrude","CAP_EDGE",EDGE,{"disambiguationData":[OSD([sQuery(id+"F9.wireOp",EDGE,"E34.left")])],"isStart":false})});
            var Q22;
            Q22=makeQuery(id+"F3.opExtrude","SWEPT_EDGE",EDGE,{"disambiguationData":[OSD([sQuery(id+"F2.wireOp",EDGE,"E5"),sQuery(id+"F2.wireOp",EDGE,"E6"),sQuery(id+"F2.wireOp",EDGE,"E17")])]});
            var Q23;
            Q23=makeQuery(id+"F3.opExtrude","CAP_EDGE",EDGE,{"disambiguationData":[OSD([sQuery(id+"F2.wireOp",EDGE,"E3"),sQuery(id+"F2.wireOp",EDGE,"E4.MirrorCS"),sQuery(id+"F2.wireOp",EDGE,"E18")])],"isStart":false});
            var Q24;
            Q24=makeQuery(id+"F3.opExtrude","CAP_EDGE",EDGE,{"disambiguationData":[OSD([sQuery(id+"F2.wireOp",EDGE,"E3"),sQuery(id+"F2.wireOp",EDGE,"E4.MirrorCS"),sQuery(id+"F2.wireOp",EDGE,"E18")])],"isStart":true});
            var Q25;
            Q25=makeQuery(id+"F3.opExtrude","SWEPT_EDGE",EDGE,{"disambiguationData":[OSD([sQuery(id+"F2.wireOp",EDGE,"E4.MirrorCS"),sQuery(id+"F2.wireOp",EDGE,"E8")])]});
            var Q26;
            Q26=makeQuery(id+"F3.opExtrude","SWEPT_EDGE",EDGE,{"disambiguationData":[OSD([sQuery(id+"F2.wireOp",EDGE,"E17"),sQuery(id+"F2.wireOp",EDGE,"E18")])]});
            var Q27;
            Q27=makeQuery(id+"F6.opChamfer","BLEND_EDGE",EDGE,{"blendedFrom":[makeQuery(id+"F3.opExtrude","CAP_EDGE",EDGE,{"disambiguationData":[OSD([sQuery(id+"F2.wireOp",EDGE,"E15.bottom")])],"isStart":false}),makeQuery(id+"F3.opExtrude","SWEPT_FACE",FACE,{"disambiguationData":[OSD([sQuery(id+"F2.wireOp",EDGE,"E23")])]})],"blendedInto":[makeQuery(id+"F3.opExtrude","SWEPT_FACE",FACE,{"disambiguationData":[OSD([sQuery(id+"F2.wireOp",EDGE,"E23")])]})]});
            var Q28;
            Q28=makeQuery(id+"F6.opChamfer","BLEND_EDGE",EDGE,{"blendedFrom":[makeQuery(id+"F3.opExtrude","CAP_EDGE",EDGE,{"disambiguationData":[OSD([sQuery(id+"F2.wireOp",EDGE,"E15.bottom")])],"isStart":true}),makeQuery(id+"F3.opExtrude","SWEPT_FACE",FACE,{"disambiguationData":[OSD([sQuery(id+"F2.wireOp",EDGE,"E23")])]})],"blendedInto":[makeQuery(id+"F3.opExtrude","SWEPT_FACE",FACE,{"disambiguationData":[OSD([sQuery(id+"F2.wireOp",EDGE,"E23")])]})]});
            chamfer(context, id + "F14", {"entities" : qUnion([Q0, Q1, Q2, Q3, Q4, Q5, Q6, Q7, Q8, Q9, Q10, Q11, Q12, Q13, Q14, Q15, Q16, Q17, Q18, Q19, Q20, Q21, Q22, Q23, Q24, Q25, Q26, Q27, Q28]), "width" : .5 * mm, "tangentPropagation" : true});
        }
        {
            var Q0;
            Q0=qCreatedBy(makeId("Right.planeOp"),FACE);
            cPlane(context, id + "F15", {"entities" : qUnion([Q0]), "cplaneType" : CPlaneType.OFFSET, "offset" : 5.5 * mm, "width" : 150 * mm, "height" : 150 * mm});
        }
        {
            var Q0;
            Q0=qCreatedBy(id+"F15.planeOp",FACE);
            var sketch = newSketch(context, id + "F16", { "sketchPlane" : qUnion([Q0])});
            skLineSegment(sketch, "E39", {"start": v(0, 0) * mm, "end": v(-1.5, 0) * mm});
            skLineSegment(sketch, "E40", {"start": v(-1.5, 0) * mm, "end": v(-1.5, 33.5) * mm});
            skLineSegment(sketch, "E41", {"start": v(-1.5, 33.5) * mm, "end": v(3.5, 33.5) * mm});
            skLineSegment(sketch, "E42", {"start": v(3.5, 33.5) * mm, "end": v(3.5, 0) * mm});
            skLineSegment(sketch, "E43", {"start": v(3.5, 0) * mm, "end": v(-1.5, 0) * mm});
            skLineSegment(sketch, "E44", {"start": v(-1.5, 0) * mm, "end": v(-1.5, 5.2) * mm});
            skLineSegment(sketch, "E45", {"start": v(-1.5, 5.2) * mm, "end": v(0.5, 5.2) * mm});
            skLineSegment(sketch, "E46", {"start": v(0.5, 5.2) * mm, "end": v(0.5, 32.7) * mm});
            skLineSegment(sketch, "E47", {"start": v(0.5, 32.7) * mm, "end": v(-1.5, 32.7) * mm});
            skLineSegment(sketch, "E48.MirrorCS", {"start": v(-3.5, 32.7) * mm, "end": v(-1.5, 32.7) * mm});
            skLineSegment(sketch, "E49.MirrorCS", {"start": v(-1.5, 33.5) * mm, "end": v(-6.5, 33.5) * mm});
            skLineSegment(sketch, "E50.MirrorCS", {"start": v(-6.5, 33.5) * mm, "end": v(-6.5, 0) * mm});
            skLineSegment(sketch, "E51", {"start": v(-6.5, 0) * mm, "end": v(-6.5, 11.1) * mm});
            skLineSegment(sketch, "E52", {"start": v(-6.5, 11.1) * mm, "end": v(-1.5, 11.1) * mm});
            skLineSegment(sketch, "E53", {"start": v(-1.5, 11.1) * mm, "end": v(-1.5, 7.7) * mm});
            skLineSegment(sketch, "E54", {"start": v(-1.5, 7.7) * mm, "end": v(-6.5, 7.7) * mm});
            skLineSegment(sketch, "E55", {"start": v(-3.5, 32.7) * mm, "end": v(-3.5, 11.1) * mm});
            skPoint(sketch, "E55.endSnap0", {"position": v(-4, 11.1) * mm});
            skLineSegment(sketch, "E56", {"start": v(3.5, 0) * mm, "end": v(3.5, 1.8) * mm});
            skLineSegment(sketch, "E57", {"start": v(3.5, 1.8) * mm, "end": v(-1.5, 1.8) * mm});
            skLineSegment(sketch, "E58", {"start": v(-1.5, 5.2) * mm, "end": v(-2.5, 5.2) * mm});
            skLineSegment(sketch, "E59.bottom", {"start": v(-2.5, 5.2) * mm, "end": v(-1.5, 5.2) * mm});
            skLineSegment(sketch, "E59.top", {"start": v(-2.5, 1.8) * mm, "end": v(-1.5, 1.8) * mm});
            skLineSegment(sketch, "E59.left", {"start": v(-2.5, 5.2) * mm, "end": v(-2.5, 1.8) * mm});
            skLineSegment(sketch, "E59.right", {"start": v(-1.5, 5.2) * mm, "end": v(-1.5, 1.8) * mm});
            skLineSegment(sketch, "E60", {"start": v(-1.5, 7.7) * mm, "end": v(-0.5, 7.7) * mm});
            skLineSegment(sketch, "E61.bottom", {"start": v(-0.5, 7.7) * mm, "end": v(-1.5, 7.7) * mm});
            skLineSegment(sketch, "E61.top", {"start": v(-0.5, 11.1) * mm, "end": v(-1.5, 11.1) * mm});
            skLineSegment(sketch, "E61.left", {"start": v(-0.5, 7.7) * mm, "end": v(-0.5, 11.1) * mm});
            skLineSegment(sketch, "E61.right", {"start": v(-1.5, 7.7) * mm, "end": v(-1.5, 11.1) * mm});
            skLineSegment(sketch, "E62", {"start": v(0.5, 32.7) * mm, "end": v(1.5, 32.7) * mm});
            skLineSegment(sketch, "E63", {"start": v(1.5, 32.7) * mm, "end": v(1.5, 31.2) * mm});
            skLineSegment(sketch, "E64", {"start": v(1.5, 31.2) * mm, "end": v(0.5, 30.2) * mm});
            skLineSegment(sketch, "E65.MirrorCS", {"start": v(-3.5, 32.7) * mm, "end": v(-4.5, 32.7) * mm});
            skLineSegment(sketch, "E66.MirrorCS", {"start": v(-4.5, 32.7) * mm, "end": v(-4.5, 31.2) * mm});
            skLineSegment(sketch, "E67.MirrorCS", {"start": v(-4.5, 31.2) * mm, "end": v(-3.5, 30.2) * mm});
            skSolve(sketch);
        }
        {
            var Q0;
            {var subQ0=sQuery(id+"F16.wireOp",EDGE,"E50.MirrorCS");Q0=makeQuery(id+"F16.imprint","IMPRINT",FACE,{"disambiguationData":[TD([[makeQuery(id+"F16.imprint","IMPRINT",EDGE,{"derivedFrom":subQ0}),1.0]])]});}
            var Q1;
            {var subQ0=sQuery(id+"F16.wireOp",EDGE,"E53");Q1=makeQuery(id+"F16.imprint","IMPRINT",FACE,{"disambiguationData":[TD([[makeQuery(id+"F16.imprint","IMPRINT",EDGE,{"derivedFrom":subQ0}),-1.0]])]});}
            var Q2;
            Q2=makeQuery(id+"F16.imprint","IMPRINT",FACE,{"disambiguationData":[TD([[makeQuery(id+"F16.imprint","IMPRINT",EDGE,{"derivedFrom":sQuery(id+"F16.wireOp",EDGE,"E41")}),-1.0]])]});
            var Q3;
            {var subQ0=sQuery(id+"F16.wireOp",EDGE,"E54");Q3=makeQuery(id+"F16.imprint","IMPRINT",FACE,{"disambiguationData":[TD([[makeQuery(id+"F16.imprint","IMPRINT",EDGE,{"derivedFrom":subQ0}),-1.0]])]});}
            var Q4;
            Q4=makeQuery(id+"F16.imprint","IMPRINT",FACE,{"disambiguationData":[TD([[makeQuery(id+"F16.imprint","IMPRINT",EDGE,{"derivedFrom":sQuery(id+"F16.wireOp",EDGE,"E59.bottom")}),-1.0]])]});
            var Q5;
            Q5=makeQuery(id+"F16.imprint","IMPRINT",FACE,{"disambiguationData":[TD([[makeQuery(id+"F16.imprint","IMPRINT",EDGE,{"derivedFrom":sQuery(id+"F16.wireOp",EDGE,"E61.bottom")}),-1.0]])]});
            extrude(context, id + "F17", {"entities" : qUnion([Q0, Q1, Q2, Q3, Q4, Q5]), "depth" : 2 * mm, "offsetDistance" : 25 * mm});
        }
        {
            var Q0;
            Q0=makeQuery(id+"F17.opExtrude","SWEPT_EDGE",EDGE,{"disambiguationData":[OSD([sQuery(id+"F16.wireOp",EDGE,"E49.MirrorCS"),sQuery(id+"F16.wireOp",EDGE,"E50.MirrorCS")])]});
            var Q1;
            Q1=makeQuery(id+"F17.opExtrude","SWEPT_EDGE",EDGE,{"disambiguationData":[OSD([sQuery(id+"F16.wireOp",EDGE,"E41"),sQuery(id+"F16.wireOp",EDGE,"E42")])]});
            var Q2;
            Q2=makeQuery(id+"F17.opExtrude","SWEPT_EDGE",EDGE,{"disambiguationData":[OSD([sQuery(id+"F16.wireOp",EDGE,"E51"),sQuery(id+"F16.wireOp",EDGE,"E54")])]});
            var Q3;
            Q3=makeQuery(id+"F17.opExtrude","SWEPT_EDGE",EDGE,{"disambiguationData":[OSD([sQuery(id+"F16.wireOp",EDGE,"E42"),sQuery(id+"F16.wireOp",EDGE,"E56"),sQuery(id+"F16.wireOp",EDGE,"E57")])]});
            chamfer(context, id + "F18", {"entities" : qUnion([Q0, Q1, Q2, Q3]), "width" : 1.6 * mm, "tangentPropagation" : true});
        }
        {
            var Q0;
            Q0=makeQuery(id+"F17.opExtrude","SWEPT_EDGE",EDGE,{"disambiguationData":[OSD([sQuery(id+"F16.wireOp",EDGE,"E65.MirrorCS"),sQuery(id+"F16.wireOp",EDGE,"E66.MirrorCS")])]});
            var Q1;
            Q1=makeQuery(id+"F17.opExtrude","SWEPT_EDGE",EDGE,{"disambiguationData":[OSD([sQuery(id+"F16.wireOp",EDGE,"E66.MirrorCS"),sQuery(id+"F16.wireOp",EDGE,"E67.MirrorCS")])]});
            var Q2;
            Q2=makeQuery(id+"F17.opExtrude","SWEPT_EDGE",EDGE,{"disambiguationData":[OSD([sQuery(id+"F16.wireOp",EDGE,"E55"),sQuery(id+"F16.wireOp",EDGE,"E67.MirrorCS")])]});
            var Q3;
            Q3=makeQuery(id+"F17.opExtrude","SWEPT_EDGE",EDGE,{"disambiguationData":[OSD([sQuery(id+"F16.wireOp",EDGE,"E46"),sQuery(id+"F16.wireOp",EDGE,"E64")])]});
            var Q4;
            Q4=makeQuery(id+"F17.opExtrude","SWEPT_EDGE",EDGE,{"disambiguationData":[OSD([sQuery(id+"F16.wireOp",EDGE,"E63"),sQuery(id+"F16.wireOp",EDGE,"E64")])]});
            var Q5;
            Q5=makeQuery(id+"F17.opExtrude","SWEPT_EDGE",EDGE,{"disambiguationData":[OSD([sQuery(id+"F16.wireOp",EDGE,"E62"),sQuery(id+"F16.wireOp",EDGE,"E63")])]});
            chamfer(context, id + "F19", {"entities" : qUnion([Q0, Q1, Q2, Q3, Q4, Q5]), "width" : .5 * mm, "tangentPropagation" : true});
        }
        {
            var Q0;
            Q0=makeQuery(id+"F3.opExtrude","SWEPT_BODY",BODY,{"disambiguationData":[OSD([sQuery(id+"F2.wireOp",EDGE,"E3"),sQuery(id+"F2.wireOp",EDGE,"E4.MirrorCS"),sQuery(id+"F2.wireOp",EDGE,"E5"),sQuery(id+"F2.wireOp",EDGE,"E6"),sQuery(id+"F2.wireOp",EDGE,"E7"),sQuery(id+"F2.wireOp",EDGE,"E8"),sQuery(id+"F2.wireOp",EDGE,"E9"),sQuery(id+"F2.wireOp",EDGE,"E11"),sQuery(id+"F2.wireOp",EDGE,"E12"),sQuery(id+"F2.wireOp",EDGE,"0akQF3o6-GRSy-sqst-GOAi-R7572j4TWCA9"),sQuery(id+"F2.wireOp",EDGE,"Rr7SK3JZ-Egbp-8AZP-2McZ-Qu5wQ8jnj7ba"),sQuery(id+"F2.wireOp",EDGE,"E15.bottom"),sQuery(id+"F2.wireOp",EDGE,"E15.left"),sQuery(id+"F2.wireOp",EDGE,"E15.right"),sQuery(id+"F2.wireOp",EDGE,"E16")])]});
            var Q1;
            Q1=makeQuery(id+"F17.opExtrude","SWEPT_BODY",BODY,{"disambiguationData":[OSD([sQuery(id+"F16.wireOp",EDGE,"E41"),sQuery(id+"F16.wireOp",EDGE,"E42"),sQuery(id+"F16.wireOp",EDGE,"E44"),sQuery(id+"F16.wireOp",EDGE,"E45"),sQuery(id+"F16.wireOp",EDGE,"E46"),sQuery(id+"F16.wireOp",EDGE,"E47"),sQuery(id+"F16.wireOp",EDGE,"E48.MirrorCS"),sQuery(id+"F16.wireOp",EDGE,"E49.MirrorCS"),sQuery(id+"F16.wireOp",EDGE,"E50.MirrorCS"),sQuery(id+"F16.wireOp",EDGE,"E51"),sQuery(id+"F16.wireOp",EDGE,"E52"),sQuery(id+"F16.wireOp",EDGE,"E53"),sQuery(id+"F16.wireOp",EDGE,"E54"),sQuery(id+"F16.wireOp",EDGE,"E55"),sQuery(id+"F16.wireOp",EDGE,"E57")])]});
            var Q2;
            Q2=sQuery(id+"F0.wireOp",EDGE,"E1.bottom");
            transform(context, id + "F20", {"entities" : qUnion([Q0, Q1]), "transformType" : TransformType.ROTATION, "transformAxis" : qUnion([Q2]), "angle" : 90 * degree, "oppositeDirection" : true, "makeCopy" : false});
        }
    });
